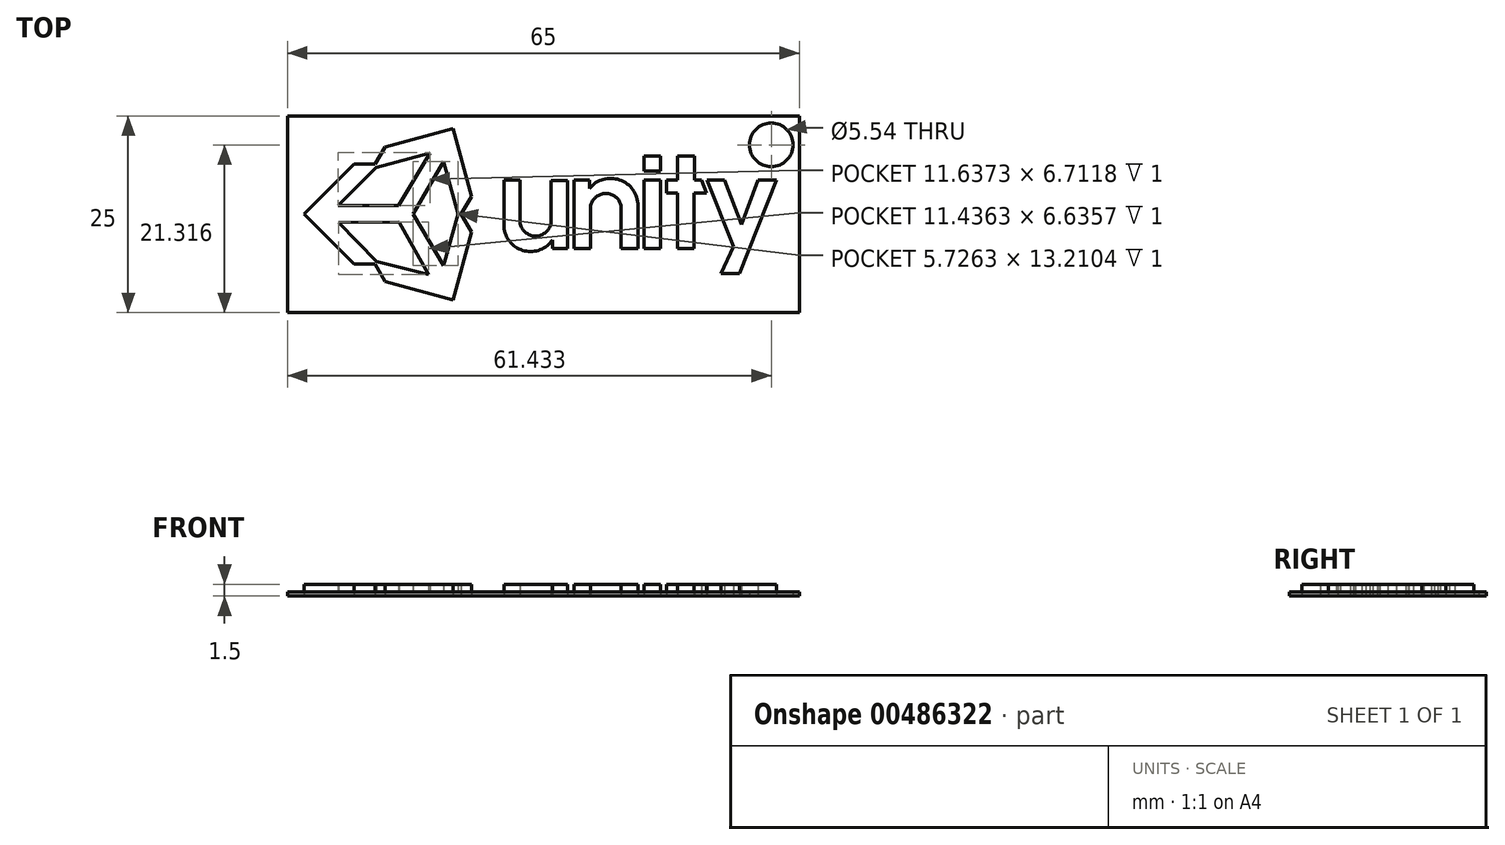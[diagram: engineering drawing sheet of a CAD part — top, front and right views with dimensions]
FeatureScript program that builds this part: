
annotation { "Feature Type Name" : "Feature", "Feature Type Description" : "" }
export const myFeature = defineFeature(function(context is Context, id is Id, definition is map)
    precondition{}
    {
        {
            var Q0;
            Q0=qCreatedBy(makeId("Top.planeOp"),FACE);
            var sketch = newSketch(context, id + "F0", { "sketchPlane" : qUnion([Q0])});
            skLineSegment(sketch, "E0", {"start": v(-27.81, 22.47) * mm, "end": v(-21.5, 16.13) * mm});
            skLineSegment(sketch, "E1", {"start": v(-21.5, 16.13) * mm, "end": v(-18.79, 16.13) * mm});
            skLineSegment(sketch, "E2", {"start": v(-18.79, 16.13) * mm, "end": v(-17.57, 13.88) * mm});
            skLineSegment(sketch, "E3", {"start": v(-17.57, 13.88) * mm, "end": v(-8.91, 11.57) * mm});
            skLineSegment(sketch, "E4", {"start": v(-8.91, 11.57) * mm, "end": v(-6.55, 20.18) * mm});
            skLineSegment(sketch, "E5", {"start": v(-6.55, 20.18) * mm, "end": v(-7.89, 22.48) * mm});
            skLineSegment(sketch, "E6", {"start": v(-7.89, 22.48) * mm, "end": v(-6.55, 24.73) * mm});
            skLineSegment(sketch, "E7", {"start": v(-6.55, 24.73) * mm, "end": v(-8.91, 33.37) * mm});
            skLineSegment(sketch, "E8", {"start": v(-8.91, 33.37) * mm, "end": v(-17.57, 31) * mm});
            skLineSegment(sketch, "E9", {"start": v(-17.57, 31) * mm, "end": v(-18.79, 28.81) * mm});
            skLineSegment(sketch, "E10", {"start": v(-18.79, 28.81) * mm, "end": v(-21.5, 28.81) * mm});
            skLineSegment(sketch, "E11", {"start": v(-21.5, 28.81) * mm, "end": v(-27.81, 22.47) * mm});
            skLineSegment(sketch, "E12", {"start": v(-23.48, 23.54) * mm, "end": v(-18.66, 28.4) * mm});
            skLineSegment(sketch, "E13", {"start": v(-18.66, 28.4) * mm, "end": v(-11.84, 30.26) * mm});
            skLineSegment(sketch, "E14", {"start": v(-11.84, 30.26) * mm, "end": v(-15.83, 23.56) * mm});
            skLineSegment(sketch, "E15", {"start": v(-15.83, 23.56) * mm, "end": v(-23.48, 23.54) * mm});
            skLineSegment(sketch, "E16", {"start": v(-23.43, 21.42) * mm, "end": v(-18.64, 16.46) * mm});
            skLineSegment(sketch, "E17", {"start": v(-18.64, 16.46) * mm, "end": v(-12, 14.8) * mm});
            skLineSegment(sketch, "E18", {"start": v(-12, 14.8) * mm, "end": v(-15.8, 21.43) * mm});
            skLineSegment(sketch, "E19", {"start": v(-15.8, 21.43) * mm, "end": v(-23.43, 21.42) * mm});
            skLineSegment(sketch, "E20", {"start": v(-14, 22.49) * mm, "end": v(-10.14, 15.93) * mm});
            skLineSegment(sketch, "E21", {"start": v(-10.14, 15.93) * mm, "end": v(-8.27, 22.47) * mm});
            skLineSegment(sketch, "E22", {"start": v(-8.27, 22.47) * mm, "end": v(-10.1, 29.14) * mm});
            skLineSegment(sketch, "E23", {"start": v(-10.1, 29.14) * mm, "end": v(-14, 22.49) * mm});
            skLineSegment(sketch, "E24", {"start": v(-2.41, 26.78) * mm, "end": v(-0.41, 26.78) * mm});
            skLineSegment(sketch, "E25", {"start": v(-0.41, 26.78) * mm, "end": v(-0.41, 21.45) * mm});
            skLineSegment(sketch, "E26", {"start": v(5.65, 26.75) * mm, "end": v(3.56, 26.75) * mm});
            skLineSegment(sketch, "E27", {"start": v(3.56, 26.75) * mm, "end": v(3.56, 21.45) * mm});
            skArc(sketch, "E28", {"start": v(-0.41, 21.45) * mm, "mid": v(1.57, 19.68) * mm, "end": v(3.56, 21.45) * mm});
            skLineSegment(sketch, "E29", {"start": v(5.65, 26.75) * mm, "end": v(5.65, 18.07) * mm});
            skLineSegment(sketch, "E30", {"start": v(5.65, 18.07) * mm, "end": v(3.71, 18.07) * mm});
            skLineSegment(sketch, "E31", {"start": v(3.71, 18.07) * mm, "end": v(3.71, 19.16) * mm});
            skLineSegment(sketch, "E32", {"start": v(-2.41, 26.78) * mm, "end": v(-2.41, 20.55) * mm});
            skArc(sketch, "E33", {"start": v(-2.41, 20.55) * mm, "mid": v(0.19, 17.8) * mm, "end": v(3.71, 19.16) * mm});
            skLineSegment(sketch, "E34", {"start": v(6.47, 26.8) * mm, "end": v(6.47, 18.07) * mm});
            skLineSegment(sketch, "E35", {"start": v(6.47, 18.07) * mm, "end": v(8.58, 18.07) * mm});
            skLineSegment(sketch, "E36", {"start": v(8.58, 18.07) * mm, "end": v(8.58, 23.55) * mm});
            skLineSegment(sketch, "E37", {"start": v(6.47, 26.8) * mm, "end": v(8.42, 26.8) * mm});
            skLineSegment(sketch, "E38", {"start": v(14.57, 18.07) * mm, "end": v(12.43, 18.07) * mm});
            skLineSegment(sketch, "E39", {"start": v(12.43, 18.07) * mm, "end": v(12.43, 23.55) * mm});
            skLineSegment(sketch, "E40", {"start": v(14.57, 18.07) * mm, "end": v(14.57, 23.55) * mm});
            skLineSegment(sketch, "E41", {"start": v(8.42, 26.8) * mm, "end": v(8.42, 25.73) * mm});
            skArc(sketch, "E42", {"start": v(12.43, 23.55) * mm, "mid": v(10.5, 25.1) * mm, "end": v(8.58, 23.55) * mm});
            skArc(sketch, "E43", {"start": v(14.57, 23.55) * mm, "mid": v(12.27, 26.81) * mm, "end": v(8.42, 25.73) * mm});
            skLineSegment(sketch, "E44", {"start": v(15.36, 26.78) * mm, "end": v(17.43, 26.78) * mm});
            skLineSegment(sketch, "E45", {"start": v(17.43, 26.78) * mm, "end": v(17.43, 18.07) * mm});
            skLineSegment(sketch, "E46", {"start": v(17.43, 18.07) * mm, "end": v(15.36, 18.07) * mm});
            skLineSegment(sketch, "E47", {"start": v(15.36, 18.07) * mm, "end": v(15.36, 26.78) * mm});
            skLineSegment(sketch, "E48", {"start": v(15.36, 29.84) * mm, "end": v(15.36, 27.96) * mm});
            skLineSegment(sketch, "E49", {"start": v(15.36, 27.96) * mm, "end": v(17.43, 27.96) * mm});
            skLineSegment(sketch, "E50", {"start": v(17.43, 27.96) * mm, "end": v(17.43, 29.84) * mm});
            skLineSegment(sketch, "E51", {"start": v(17.43, 29.84) * mm, "end": v(15.36, 29.84) * mm});
            skLineSegment(sketch, "E52", {"start": v(19.62, 29.84) * mm, "end": v(19.62, 26.78) * mm});
            skLineSegment(sketch, "E53", {"start": v(19.62, 26.78) * mm, "end": v(18.22, 26.78) * mm});
            skLineSegment(sketch, "E54", {"start": v(18.22, 26.78) * mm, "end": v(18.22, 25.17) * mm});
            skLineSegment(sketch, "E55", {"start": v(18.22, 25.17) * mm, "end": v(19.62, 25.17) * mm});
            skLineSegment(sketch, "E56", {"start": v(19.62, 25.17) * mm, "end": v(19.62, 18.07) * mm});
            skLineSegment(sketch, "E57", {"start": v(19.62, 18.07) * mm, "end": v(21.71, 18.07) * mm});
            skLineSegment(sketch, "E58", {"start": v(21.71, 18.07) * mm, "end": v(21.71, 25.17) * mm});
            skLineSegment(sketch, "E59", {"start": v(21.71, 25.17) * mm, "end": v(23.26, 25.17) * mm});
            skLineSegment(sketch, "E60", {"start": v(23.26, 25.17) * mm, "end": v(22.63, 26.78) * mm});
            skLineSegment(sketch, "E61", {"start": v(22.63, 26.78) * mm, "end": v(21.78, 26.78) * mm});
            skLineSegment(sketch, "E62", {"start": v(21.78, 26.78) * mm, "end": v(21.78, 29.84) * mm});
            skLineSegment(sketch, "E63", {"start": v(21.78, 29.84) * mm, "end": v(19.62, 29.84) * mm});
            skLineSegment(sketch, "E64", {"start": v(23.36, 26.78) * mm, "end": v(25.56, 26.78) * mm});
            skLineSegment(sketch, "E65", {"start": v(25.56, 26.78) * mm, "end": v(27.7, 21.12) * mm});
            skLineSegment(sketch, "E66", {"start": v(27.7, 21.12) * mm, "end": v(29.84, 26.78) * mm});
            skLineSegment(sketch, "E67", {"start": v(29.84, 26.78) * mm, "end": v(32.19, 26.78) * mm});
            skLineSegment(sketch, "E68", {"start": v(32.19, 26.78) * mm, "end": v(27.46, 14.94) * mm});
            skLineSegment(sketch, "E69", {"start": v(27.46, 14.94) * mm, "end": v(25.15, 14.94) * mm});
            skLineSegment(sketch, "E70", {"start": v(25.15, 14.94) * mm, "end": v(26.71, 18.32) * mm});
            skLineSegment(sketch, "E71", {"start": v(26.71, 18.32) * mm, "end": v(23.36, 26.78) * mm});
            skSolve(sketch);
        }
        {
            var Q0;
            Q0 = qSketchRegion(id + "F0", true);
            extrude(context, id + "F1", {"entities" : qUnion([Q0]), "depth" : 1.5 * mm, "offsetDistance" : 25 * mm});
        }
        {
            var Q0;
            Q0=makeQuery(id+"F0.imprint","IMPRINT",FACE,{"disambiguationData":[TD([[makeQuery(id+"F0.imprint","IMPRINT",EDGE,{"derivedFrom":sQuery(id+"F0.wireOp",EDGE,"E12")}),-1.0]])]});
            var Q1;
            Q1=makeQuery(id+"F0.imprint","IMPRINT",FACE,{"disambiguationData":[TD([[makeQuery(id+"F0.imprint","IMPRINT",EDGE,{"derivedFrom":sQuery(id+"F0.wireOp",EDGE,"E20")}),1.0]])]});
            var Q2;
            Q2=makeQuery(id+"F0.imprint","IMPRINT",FACE,{"disambiguationData":[TD([[makeQuery(id+"F0.imprint","IMPRINT",EDGE,{"derivedFrom":sQuery(id+"F0.wireOp",EDGE,"E16")}),1.0]])]});
            extrude(context, id + "F2", {"entities" : qUnion([Q0, Q1, Q2]), "operationType" : NewBodyOperationType.ADD, "depth" : .5 * mm, "offsetDistance" : 25 * mm});
        }
        {
            var Q0;
            Q0=qCreatedBy(makeId("Top.planeOp"),FACE);
            var sketch = newSketch(context, id + "F3", { "sketchPlane" : qUnion([Q0])});
            skLineSegment(sketch, "E72.bottom", {"start": v(-29.92, 34.95) * mm, "end": v(35.08, 34.95) * mm});
            skLineSegment(sketch, "E72.top", {"start": v(-29.92, 9.95) * mm, "end": v(35.08, 9.95) * mm});
            skLineSegment(sketch, "E72.left", {"start": v(-29.92, 34.95) * mm, "end": v(-29.92, 9.95) * mm});
            skLineSegment(sketch, "E72.right", {"start": v(35.08, 34.95) * mm, "end": v(35.08, 9.95) * mm});
            skCircle(sketch, "E73", {"center": v(31.51, 31.27) * mm, "radius": 2.77 * mm});
            skSolve(sketch);
        }
        {
            var Q0;
            Q0 = qSketchRegion(id + "F3", true);
            extrude(context, id + "F4", {"entities" : qUnion([Q0]), "depth" : .5 * mm, "offsetDistance" : 25 * mm});
        }
    });
